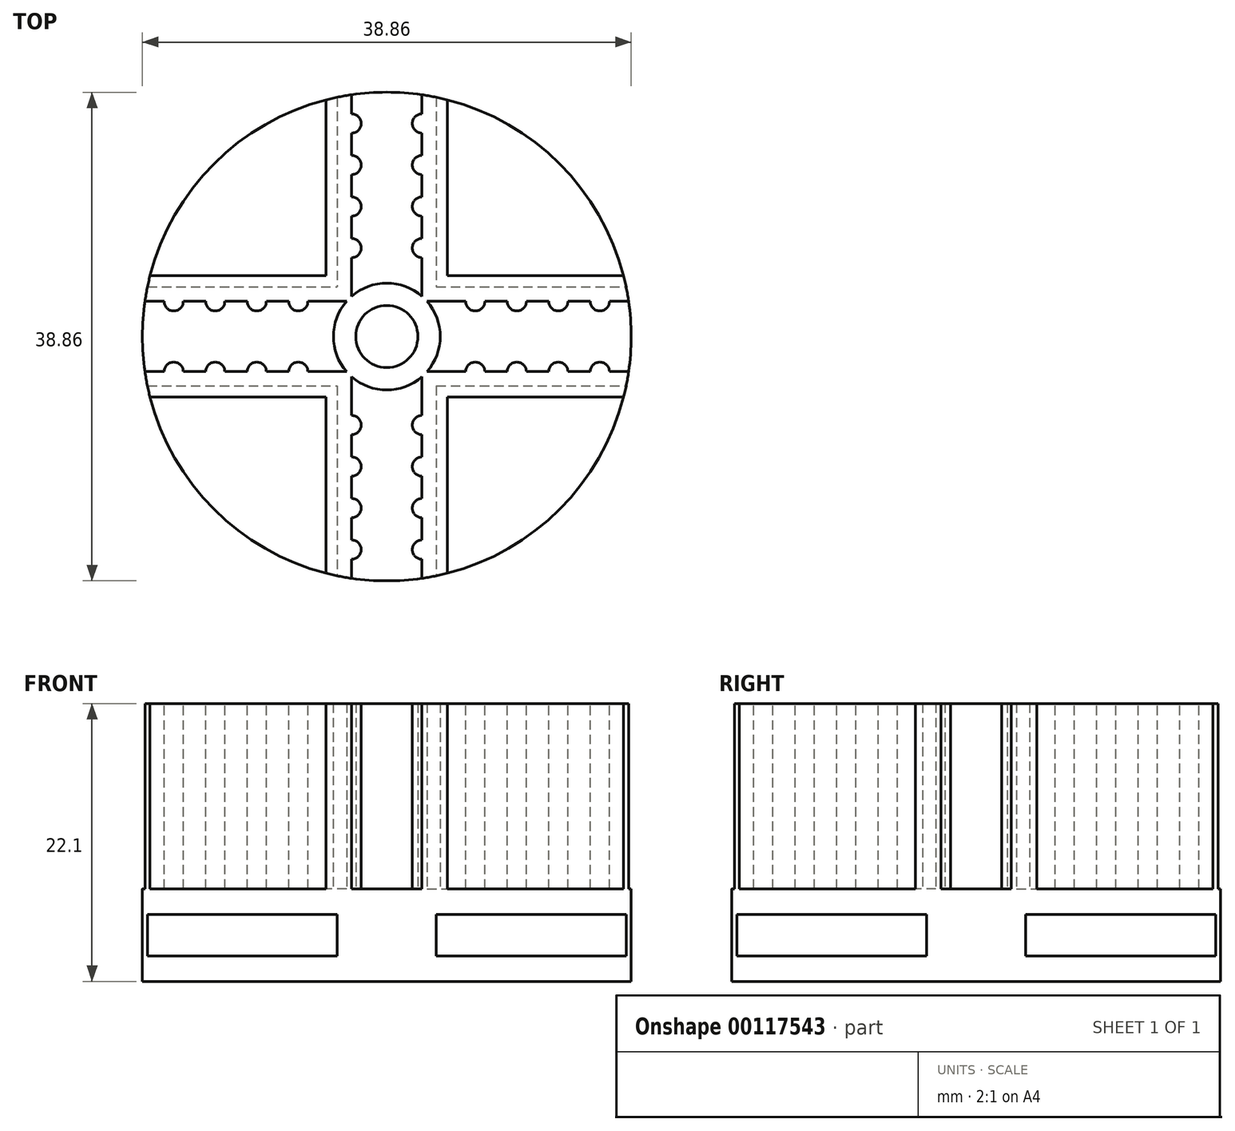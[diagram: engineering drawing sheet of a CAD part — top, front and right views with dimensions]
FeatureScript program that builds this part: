
annotation { "Feature Type Name" : "Feature", "Feature Type Description" : "" }
export const myFeature = defineFeature(function(context is Context, id is Id, definition is map)
    precondition{}
    {
        {
            var Q0;
            Q0=qCreatedBy(makeId("Top.planeOp"),FACE);
            var sketch = newSketch(context, id + "F0", { "sketchPlane" : qUnion([Q0])});
            skCircle(sketch, "E0", {"center": v(0, 0) * mm, "radius": 19.43 * mm});
            skSolve(sketch);
        }
        {
            var Q0;
            Q0 = qSketchRegion(id + "F0", true);
            extrude(context, id + "F1", {"entities" : qUnion([Q0]), "depth" : 2.03 * mm});
        }
        {
            var Q0;
            Q0=makeQuery(id+"F1.opExtrude","CAP_FACE",FACE,{"disambiguationData":[OSD([sQuery(id+"F0.wireOp",EDGE,"E0")])],"isStart":false});
            var sketch = newSketch(context, id + "F2", { "sketchPlane" : qUnion([Q0])});
            skLineSegment(sketch, "E1.left", {"start": v(3.94, 19.03) * mm, "end": v(3.94, 3.94) * mm});
            skLineSegment(sketch, "E1.right", {"start": v(-3.94, 19.03) * mm, "end": v(-3.94, 3.94) * mm});
            skPoint(sketch, "E1.middle", {"position": v(0, 0) * mm});
            skLineSegment(sketch, "E2.bottom", {"start": v(-19.03, 3.94) * mm, "end": v(-3.94, 3.94) * mm});
            skLineSegment(sketch, "E2.top", {"start": v(-19.03, -3.94) * mm, "end": v(-3.94, -3.94) * mm});
            skArc(sketch, "E3.0", {"start": v(19.03, -3.94) * mm, "mid": v(19.43, 0) * mm, "end": v(19.03, 3.94) * mm});
            skLineSegment(sketch, "E4.trimOffspring", {"start": v(3.94, 3.94) * mm, "end": v(19.03, 3.94) * mm});
            skLineSegment(sketch, "E5.trimOffspring", {"start": v(3.94, -3.94) * mm, "end": v(3.94, -19.03) * mm});
            skLineSegment(sketch, "E6.trimOffspring", {"start": v(3.94, -3.94) * mm, "end": v(19.03, -3.94) * mm});
            skLineSegment(sketch, "E7.trimOffspring", {"start": v(-3.94, -3.94) * mm, "end": v(-3.94, -19.03) * mm});
            skArc(sketch, "E8.trimOffspring", {"start": v(3.94, 19.03) * mm, "mid": v(0, 19.43) * mm, "end": v(-3.94, 19.03) * mm});
            skArc(sketch, "E9.trimOffspring", {"start": v(-19.03, 3.94) * mm, "mid": v(-19.43, 0) * mm, "end": v(-19.03, -3.94) * mm});
            skArc(sketch, "E10.trimOffspring", {"start": v(-3.94, -19.03) * mm, "mid": v(0, -19.43) * mm, "end": v(3.94, -19.03) * mm});
            skPoint(sketch, "E11.orphan", {"position": v(-24.75, 3.94) * mm});
            skPoint(sketch, "E12.orphan", {"position": v(-24.75, -3.94) * mm});
            skPoint(sketch, "E1.top.end.orphan", {"position": v(-3.94, -23.72) * mm});
            skPoint(sketch, "E1.top.start.orphan", {"position": v(3.94, -23.72) * mm});
            skPoint(sketch, "E13.orphan", {"position": v(24.75, -3.94) * mm});
            skPoint(sketch, "E14.orphan", {"position": v(24.75, 3.94) * mm});
            skPoint(sketch, "E1.bottom.start.orphan", {"position": v(3.94, 23.72) * mm});
            skPoint(sketch, "E15.orphan", {"position": v(-3.94, 23.72) * mm});
            skLineSegment(sketch, "E16", {"start": v(0, 0) * mm, "end": v(0, 24.04) * mm, "construction": true});
            skPoint(sketch, "E16.endSnap0", {"position": v(0, 19.43) * mm});
            skLineSegment(sketch, "E17", {"start": v(0, 0) * mm, "end": v(36.17, 0) * mm, "construction": true});
            skSolve(sketch);
        }
        {
            var Q0;
            Q0 = qSketchRegion(id + "F2", true);
            extrude(context, id + "F3", {"entities" : qUnion([Q0]), "operationType" : NewBodyOperationType.ADD, "depth" : 5.33 * mm});
        }
        {
            var Q0;
            Q0=makeQuery(id+"F3.opExtrude","CAP_FACE",FACE,{"disambiguationData":[OSD([sQuery(id+"F2.wireOp",EDGE,"E1.left"),sQuery(id+"F2.wireOp",EDGE,"E1.right"),sQuery(id+"F2.wireOp",EDGE,"E2.bottom"),sQuery(id+"F2.wireOp",EDGE,"E2.top"),sQuery(id+"F2.wireOp",EDGE,"E3.0"),sQuery(id+"F2.wireOp",EDGE,"E4.trimOffspring"),sQuery(id+"F2.wireOp",EDGE,"E5.trimOffspring"),sQuery(id+"F2.wireOp",EDGE,"E6.trimOffspring"),sQuery(id+"F2.wireOp",EDGE,"E7.trimOffspring"),sQuery(id+"F2.wireOp",EDGE,"E8.trimOffspring"),sQuery(id+"F2.wireOp",EDGE,"E9.trimOffspring"),sQuery(id+"F2.wireOp",EDGE,"E10.trimOffspring")])],"isStart":false});
            var sketch = newSketch(context, id + "F4", { "sketchPlane" : qUnion([Q0])});
            skPoint(sketch, "E18.center", {"position": v(0, 0) * mm});
            skPoint(sketch, "E19.center", {"position": v(0.66, 0.64) * mm});
            skLineSegment(sketch, "E20", {"start": v(2.8, 19.23) * mm, "end": v(2.8, 2.8) * mm});
            skLineSegment(sketch, "E21", {"start": v(2.8, 2.8) * mm, "end": v(19.23, 2.8) * mm});
            skLineSegment(sketch, "E22", {"start": v(18.82, 4.83) * mm, "end": v(4.83, 4.83) * mm});
            skLineSegment(sketch, "E23", {"start": v(4.83, 4.83) * mm, "end": v(4.83, 18.82) * mm});
            skArc(sketch, "E24.0", {"start": v(19.03, 3.94) * mm, "mid": v(18.93, 4.38) * mm, "end": v(18.82, 4.83) * mm});
            skArc(sketch, "E25.0", {"start": v(3.94, 19.03) * mm, "mid": v(3.37, 19.14) * mm, "end": v(2.8, 19.23) * mm});
            skArc(sketch, "E26.0", {"start": v(19.23, 2.8) * mm, "mid": v(19.14, 3.37) * mm, "end": v(19.03, 3.94) * mm});
            skPoint(sketch, "E27.orphan", {"position": v(-3.94, 19.03) * mm});
            skArc(sketch, "E28.trimOffspring", {"start": v(4.83, 18.82) * mm, "mid": v(4.38, 18.93) * mm, "end": v(3.94, 19.03) * mm});
            skPoint(sketch, "E29.orphan", {"position": v(19.03, -3.94) * mm});
            skLineSegment(sketch, "E30.1.0", {"start": v(-4.83, 18.82) * mm, "end": v(-4.83, 4.83) * mm});
            skLineSegment(sketch, "E30.1.1", {"start": v(-2.8, 2.8) * mm, "end": v(-2.8, 19.23) * mm});
            skLineSegment(sketch, "E30.1.2", {"start": v(-4.83, 4.83) * mm, "end": v(-18.82, 4.83) * mm});
            skLineSegment(sketch, "E30.1.3", {"start": v(-19.23, 2.8) * mm, "end": v(-2.8, 2.8) * mm});
            skArc(sketch, "E30.1.4", {"start": v(-18.82, 4.83) * mm, "mid": v(-18.93, 4.38) * mm, "end": v(-19.03, 3.94) * mm});
            skArc(sketch, "E30.1.5", {"start": v(-2.8, 19.23) * mm, "mid": v(-3.37, 19.14) * mm, "end": v(-3.94, 19.03) * mm});
            skArc(sketch, "E30.1.6", {"start": v(-3.94, 19.03) * mm, "mid": v(-4.38, 18.93) * mm, "end": v(-4.83, 18.82) * mm});
            skArc(sketch, "E30.1.7", {"start": v(-19.03, 3.94) * mm, "mid": v(-19.14, 3.37) * mm, "end": v(-19.23, 2.8) * mm});
            skLineSegment(sketch, "E30.2.0", {"start": v(-18.82, -4.83) * mm, "end": v(-4.83, -4.83) * mm});
            skLineSegment(sketch, "E30.2.1", {"start": v(-2.8, -2.8) * mm, "end": v(-19.23, -2.8) * mm});
            skLineSegment(sketch, "E30.2.2", {"start": v(-4.83, -4.83) * mm, "end": v(-4.83, -18.82) * mm});
            skLineSegment(sketch, "E30.2.3", {"start": v(-2.8, -19.23) * mm, "end": v(-2.8, -2.8) * mm});
            skArc(sketch, "E30.2.4", {"start": v(-4.83, -18.82) * mm, "mid": v(-4.38, -18.93) * mm, "end": v(-3.94, -19.03) * mm});
            skArc(sketch, "E30.2.5", {"start": v(-19.23, -2.8) * mm, "mid": v(-19.14, -3.37) * mm, "end": v(-19.03, -3.94) * mm});
            skArc(sketch, "E30.2.6", {"start": v(-19.03, -3.94) * mm, "mid": v(-18.93, -4.38) * mm, "end": v(-18.82, -4.83) * mm});
            skArc(sketch, "E30.2.7", {"start": v(-3.94, -19.03) * mm, "mid": v(-3.37, -19.14) * mm, "end": v(-2.8, -19.23) * mm});
            skLineSegment(sketch, "E30.3.0", {"start": v(4.83, -18.82) * mm, "end": v(4.83, -4.83) * mm});
            skLineSegment(sketch, "E30.3.1", {"start": v(2.8, -2.8) * mm, "end": v(2.8, -19.23) * mm});
            skLineSegment(sketch, "E30.3.2", {"start": v(4.83, -4.83) * mm, "end": v(18.82, -4.83) * mm});
            skLineSegment(sketch, "E30.3.3", {"start": v(19.23, -2.8) * mm, "end": v(2.8, -2.8) * mm});
            skArc(sketch, "E30.3.4", {"start": v(18.82, -4.83) * mm, "mid": v(18.93, -4.38) * mm, "end": v(19.03, -3.94) * mm});
            skArc(sketch, "E30.3.5", {"start": v(2.8, -19.23) * mm, "mid": v(3.37, -19.14) * mm, "end": v(3.94, -19.03) * mm});
            skArc(sketch, "E30.3.6", {"start": v(3.94, -19.03) * mm, "mid": v(4.38, -18.93) * mm, "end": v(4.83, -18.82) * mm});
            skArc(sketch, "E30.3.7", {"start": v(19.03, -3.94) * mm, "mid": v(19.14, -3.37) * mm, "end": v(19.23, -2.8) * mm});
            skSolve(sketch);
        }
        {
            var Q0;
            Q0 = qSketchRegion(id + "F4", true);
            extrude(context, id + "F5", {"entities" : qUnion([Q0]), "operationType" : NewBodyOperationType.ADD, "depth" : 14.73 * mm});
        }
        {
            var Q0;
            Q0=makeQuery(id+"F3.opExtrude","CAP_FACE",FACE,{"disambiguationData":[OSD([sQuery(id+"F2.wireOp",EDGE,"E1.left"),sQuery(id+"F2.wireOp",EDGE,"E1.right"),sQuery(id+"F2.wireOp",EDGE,"E2.bottom"),sQuery(id+"F2.wireOp",EDGE,"E2.top"),sQuery(id+"F2.wireOp",EDGE,"E3.0"),sQuery(id+"F2.wireOp",EDGE,"E4.trimOffspring"),sQuery(id+"F2.wireOp",EDGE,"E5.trimOffspring"),sQuery(id+"F2.wireOp",EDGE,"E6.trimOffspring"),sQuery(id+"F2.wireOp",EDGE,"E7.trimOffspring"),sQuery(id+"F2.wireOp",EDGE,"E8.trimOffspring"),sQuery(id+"F2.wireOp",EDGE,"E9.trimOffspring"),sQuery(id+"F2.wireOp",EDGE,"E10.trimOffspring")])],"isStart":false});
            var sketch = newSketch(context, id + "F6", { "sketchPlane" : qUnion([Q0])});
            skCircle(sketch, "E31", {"center": v(0, 0) * mm, "radius": 2.47 * mm});
            skCircle(sketch, "E32", {"center": v(0, 0) * mm, "radius": 4.25 * mm});
            skSolve(sketch);
        }
        {
            var Q0;
            Q0 = qSketchRegion(id + "F6", true);
            var Q1;
            Q1=makeQuery(id+"F5.opExtrude","CAP_FACE",FACE,{"disambiguationData":[OSD([sQuery(id+"F4.wireOp",EDGE,"E30.1.0"),sQuery(id+"F4.wireOp",EDGE,"E30.1.1"),sQuery(id+"F4.wireOp",EDGE,"E30.1.2"),sQuery(id+"F4.wireOp",EDGE,"E30.1.3"),sQuery(id+"F4.wireOp",EDGE,"E30.1.4"),sQuery(id+"F4.wireOp",EDGE,"E30.1.5"),sQuery(id+"F4.wireOp",EDGE,"E30.1.6"),sQuery(id+"F4.wireOp",EDGE,"E30.1.7")])],"isStart":false});
            extrude(context, id + "F7", {"entities" : qUnion([Q0]), "operationType" : NewBodyOperationType.ADD, "endBound" : BoundingType.UP_TO_SURFACE, "endBoundEntityFace" : qUnion([Q1]), "depth" : 25.4 * mm});
        }
        {
            var Q0;
            Q0=makeQuery(id+"F5.opExtrude","CAP_FACE",FACE,{"disambiguationData":[OSD([sQuery(id+"F4.wireOp",EDGE,"E20"),sQuery(id+"F4.wireOp",EDGE,"E21"),sQuery(id+"F4.wireOp",EDGE,"E22"),sQuery(id+"F4.wireOp",EDGE,"E23"),sQuery(id+"F4.wireOp",EDGE,"E24.0"),sQuery(id+"F4.wireOp",EDGE,"E25.0"),sQuery(id+"F4.wireOp",EDGE,"E26.0"),sQuery(id+"F4.wireOp",EDGE,"E28.trimOffspring")])],"isStart":true});
            var sketch = newSketch(context, id + "F8", { "sketchPlane" : qUnion([Q0])});
            skLineSegment(sketch, "E33.0.0", {"start": v(-3.94, 19.03) * mm, "end": v(-3.94, 3.94) * mm});
            skLineSegment(sketch, "E33.0.1", {"start": v(-3.94, 3.94) * mm, "end": v(-19.03, 3.94) * mm});
            skArc(sketch, "E33.0.2", {"start": v(-19.03, 3.94) * mm, "mid": v(-13.74, 13.74) * mm, "end": v(-3.94, 19.03) * mm});
            skArc(sketch, "E34.1.0", {"start": v(-3.94, -19.03) * mm, "mid": v(-13.74, -13.74) * mm, "end": v(-19.03, -3.94) * mm});
            skLineSegment(sketch, "E34.1.1", {"start": v(-3.94, -3.94) * mm, "end": v(-3.94, -19.03) * mm});
            skLineSegment(sketch, "E34.1.2", {"start": v(-19.03, -3.94) * mm, "end": v(-3.94, -3.94) * mm});
            skArc(sketch, "E34.2.0", {"start": v(19.03, -3.94) * mm, "mid": v(13.74, -13.74) * mm, "end": v(3.94, -19.03) * mm});
            skLineSegment(sketch, "E34.2.1", {"start": v(3.94, -3.94) * mm, "end": v(19.03, -3.94) * mm});
            skLineSegment(sketch, "E34.2.2", {"start": v(3.94, -19.03) * mm, "end": v(3.94, -3.94) * mm});
            skArc(sketch, "E34.3.0", {"start": v(3.94, 19.03) * mm, "mid": v(13.74, 13.74) * mm, "end": v(19.03, 3.94) * mm});
            skLineSegment(sketch, "E34.3.1", {"start": v(3.94, 3.94) * mm, "end": v(3.94, 19.03) * mm});
            skLineSegment(sketch, "E34.3.2", {"start": v(19.03, 3.94) * mm, "end": v(3.94, 3.94) * mm});
            skSolve(sketch);
        }
        {
            var Q0;
            Q0 = qSketchRegion(id + "F8", true);
            extrude(context, id + "F9", {"entities" : qUnion([Q0]), "operationType" : NewBodyOperationType.ADD, "depth" : 2.03 * mm});
        }
        {
            var Q0;
            {var subQ0=sQuery(id+"F4.wireOp",EDGE,"E30.1.7");var subQ1=sQuery(id+"F4.wireOp",EDGE,"E30.1.6");var subQ2=sQuery(id+"F4.wireOp",EDGE,"E30.1.5");var subQ3=sQuery(id+"F4.wireOp",EDGE,"E30.1.4");var subQ4=sQuery(id+"F4.wireOp",EDGE,"E30.1.3");var subQ5=sQuery(id+"F4.wireOp",EDGE,"E30.1.2");var subQ6=sQuery(id+"F4.wireOp",EDGE,"E30.1.1");var subQ7=sQuery(id+"F4.wireOp",EDGE,"E30.1.0");Q0=makeQuery(id+"F7.boolean.opBoolean","MERGE",FACE,{"derivedFrom":[makeQuery(id+"F5.opExtrude","CAP_FACE",FACE,{"disambiguationData":[OSD([sQuery(id+"F4.wireOp",EDGE,"E20"),sQuery(id+"F4.wireOp",EDGE,"E21"),sQuery(id+"F4.wireOp",EDGE,"E22"),sQuery(id+"F4.wireOp",EDGE,"E23"),sQuery(id+"F4.wireOp",EDGE,"E24.0"),sQuery(id+"F4.wireOp",EDGE,"E25.0"),sQuery(id+"F4.wireOp",EDGE,"E26.0"),sQuery(id+"F4.wireOp",EDGE,"E28.trimOffspring")])],"isStart":false}),makeQuery(id+"F5.opExtrude","CAP_FACE",FACE,{"disambiguationData":[OSD([subQ7,subQ6,subQ5,subQ4,subQ3,subQ2,subQ1,subQ0])],"isStart":false}),makeQuery(id+"F5.opExtrude","CAP_FACE",FACE,{"disambiguationData":[OSD([sQuery(id+"F4.wireOp",EDGE,"E30.2.0"),sQuery(id+"F4.wireOp",EDGE,"E30.2.1"),sQuery(id+"F4.wireOp",EDGE,"E30.2.2"),sQuery(id+"F4.wireOp",EDGE,"E30.2.3"),sQuery(id+"F4.wireOp",EDGE,"E30.2.4"),sQuery(id+"F4.wireOp",EDGE,"E30.2.5"),sQuery(id+"F4.wireOp",EDGE,"E30.2.6"),sQuery(id+"F4.wireOp",EDGE,"E30.2.7")])],"isStart":false}),makeQuery(id+"F5.opExtrude","CAP_FACE",FACE,{"disambiguationData":[OSD([sQuery(id+"F4.wireOp",EDGE,"E30.3.0"),sQuery(id+"F4.wireOp",EDGE,"E30.3.1"),sQuery(id+"F4.wireOp",EDGE,"E30.3.2"),sQuery(id+"F4.wireOp",EDGE,"E30.3.3"),sQuery(id+"F4.wireOp",EDGE,"E30.3.4"),sQuery(id+"F4.wireOp",EDGE,"E30.3.5"),sQuery(id+"F4.wireOp",EDGE,"E30.3.6"),sQuery(id+"F4.wireOp",EDGE,"E30.3.7")])],"isStart":false}),makeQuery(id+"F7.opExtrude","CAP_FACE",FACE,{"disambiguationData":[OSD([subQ7,subQ6,subQ5,subQ4,subQ3,subQ2,subQ1,subQ0])],"isStart":false})]});}
            var sketch = newSketch(context, id + "F10", { "sketchPlane" : qUnion([Q0])});
            skLineSegment(sketch, "E35.0", {"start": v(17.7, -2.8) * mm, "end": v(16.18, -2.8) * mm});
            skArc(sketch, "E36", {"start": v(17.7, -2.8) * mm, "mid": v(16.94, -2.03) * mm, "end": v(16.18, -2.8) * mm});
            skPoint(sketch, "E37.orphan", {"position": v(19.23, -2.8) * mm});
            skPoint(sketch, "E38.orphan", {"position": v(3.2, -2.8) * mm});
            skArc(sketch, "E39.1.0.0", {"start": v(14.4, -2.8) * mm, "mid": v(13.64, -2.03) * mm, "end": v(12.88, -2.8) * mm});
            skPoint(sketch, "E39.1.0.1", {"position": v(15.93, -2.8) * mm});
            skLineSegment(sketch, "E39.1.0.2", {"start": v(14.4, -2.8) * mm, "end": v(12.88, -2.8) * mm});
            skArc(sketch, "E39.2.0.0", {"start": v(11.1, -2.8) * mm, "mid": v(10.34, -2.03) * mm, "end": v(9.58, -2.8) * mm});
            skPoint(sketch, "E39.2.0.1", {"position": v(12.63, -2.8) * mm});
            skLineSegment(sketch, "E39.2.0.2", {"start": v(11.1, -2.8) * mm, "end": v(9.58, -2.8) * mm});
            skArc(sketch, "E39.3.0.0", {"start": v(7.8, -2.8) * mm, "mid": v(7.04, -2.03) * mm, "end": v(6.28, -2.8) * mm});
            skPoint(sketch, "E39.3.0.1", {"position": v(9.32, -2.8) * mm});
            skLineSegment(sketch, "E39.3.0.2", {"start": v(7.8, -2.8) * mm, "end": v(6.28, -2.8) * mm});
            skLineSegment(sketch, "E39.direction1", {"start": v(16.18, -2.8) * mm, "end": v(12.88, -2.8) * mm, "construction": true});
            skLineSegment(sketch, "E40", {"start": v(0, 0) * mm, "end": v(26.06, 0) * mm, "construction": true});
            skLineSegment(sketch, "E41.MirrorCS", {"start": v(17.7, 2.8) * mm, "end": v(16.18, 2.8) * mm});
            skLineSegment(sketch, "E42.MirrorCS", {"start": v(7.8, 2.8) * mm, "end": v(6.28, 2.8) * mm});
            skLineSegment(sketch, "E43.MirrorCS", {"start": v(14.4, 2.8) * mm, "end": v(12.88, 2.8) * mm});
            skLineSegment(sketch, "E44.MirrorCS", {"start": v(11.1, 2.8) * mm, "end": v(9.58, 2.8) * mm});
            skArc(sketch, "E45.MirrorCS", {"start": v(17.7, 2.8) * mm, "mid": v(16.94, 2.03) * mm, "end": v(16.18, 2.8) * mm});
            skPoint(sketch, "E46.MirrorP", {"position": v(15.93, 2.8) * mm});
            skPoint(sketch, "E47.MirrorP", {"position": v(12.63, 2.8) * mm});
            skPoint(sketch, "E48.MirrorP", {"position": v(19.23, 2.8) * mm});
            skArc(sketch, "E49.MirrorCS", {"start": v(11.1, 2.8) * mm, "mid": v(10.34, 2.03) * mm, "end": v(9.58, 2.8) * mm});
            skPoint(sketch, "E50.MirrorP", {"position": v(9.32, 2.8) * mm});
            skLineSegment(sketch, "E51.MirrorCS", {"start": v(16.18, 2.8) * mm, "end": v(12.88, 2.8) * mm, "construction": true});
            skArc(sketch, "E52.MirrorCS", {"start": v(14.4, 2.8) * mm, "mid": v(13.64, 2.03) * mm, "end": v(12.88, 2.8) * mm});
            skArc(sketch, "E53.MirrorCS", {"start": v(7.8, 2.8) * mm, "mid": v(7.04, 2.03) * mm, "end": v(6.28, 2.8) * mm});
            skLineSegment(sketch, "E54.1.0", {"start": v(-2.8, 16.18) * mm, "end": v(-2.8, 12.88) * mm, "construction": true});
            skPoint(sketch, "E54.1.1", {"position": v(2.8, 19.23) * mm});
            skArc(sketch, "E54.1.2", {"start": v(2.8, 11.1) * mm, "mid": v(2.03, 10.34) * mm, "end": v(2.8, 9.58) * mm});
            skPoint(sketch, "E54.1.3", {"position": v(2.8, 15.93) * mm});
            skArc(sketch, "E54.1.4", {"start": v(-2.8, 11.1) * mm, "mid": v(-2.03, 10.34) * mm, "end": v(-2.8, 9.58) * mm});
            skArc(sketch, "E54.1.5", {"start": v(2.8, 7.8) * mm, "mid": v(2.03, 7.04) * mm, "end": v(2.8, 6.28) * mm});
            skArc(sketch, "E54.1.6", {"start": v(2.8, 17.7) * mm, "mid": v(2.03, 16.94) * mm, "end": v(2.8, 16.18) * mm});
            skPoint(sketch, "E54.1.7", {"position": v(2.8, 9.32) * mm});
            skPoint(sketch, "E54.1.8", {"position": v(-2.8, 12.63) * mm});
            skArc(sketch, "E54.1.9", {"start": v(-2.8, 17.7) * mm, "mid": v(-2.03, 16.94) * mm, "end": v(-2.8, 16.18) * mm});
            skPoint(sketch, "E54.1.10", {"position": v(-2.8, 19.23) * mm});
            skPoint(sketch, "E54.1.11", {"position": v(2.8, 12.63) * mm});
            skLineSegment(sketch, "E54.1.12", {"start": v(0, 0) * mm, "end": v(0, 26.06) * mm, "construction": true});
            skPoint(sketch, "E54.1.13", {"position": v(-2.8, 9.32) * mm});
            skArc(sketch, "E54.1.14", {"start": v(-2.8, 7.8) * mm, "mid": v(-2.03, 7.04) * mm, "end": v(-2.8, 6.28) * mm});
            skArc(sketch, "E54.1.15", {"start": v(2.8, 14.4) * mm, "mid": v(2.03, 13.64) * mm, "end": v(2.8, 12.88) * mm});
            skLineSegment(sketch, "E54.1.16", {"start": v(2.8, 16.18) * mm, "end": v(2.8, 12.88) * mm, "construction": true});
            skArc(sketch, "E54.1.17", {"start": v(-2.8, 14.4) * mm, "mid": v(-2.03, 13.64) * mm, "end": v(-2.8, 12.88) * mm});
            skPoint(sketch, "E54.1.18", {"position": v(-2.8, 15.93) * mm});
            skLineSegment(sketch, "E54.1.19", {"start": v(2.8, 11.1) * mm, "end": v(2.8, 9.58) * mm});
            skLineSegment(sketch, "E54.1.20", {"start": v(-2.8, 17.7) * mm, "end": v(-2.8, 16.18) * mm});
            skLineSegment(sketch, "E54.1.21", {"start": v(-2.8, 7.8) * mm, "end": v(-2.8, 6.28) * mm});
            skLineSegment(sketch, "E54.1.22", {"start": v(-2.8, 14.4) * mm, "end": v(-2.8, 12.88) * mm});
            skLineSegment(sketch, "E54.1.23", {"start": v(2.8, 17.7) * mm, "end": v(2.8, 16.18) * mm});
            skLineSegment(sketch, "E54.1.24", {"start": v(-2.8, 11.1) * mm, "end": v(-2.8, 9.58) * mm});
            skLineSegment(sketch, "E54.1.25", {"start": v(2.8, 14.4) * mm, "end": v(2.8, 12.88) * mm});
            skLineSegment(sketch, "E54.1.26", {"start": v(2.8, 7.8) * mm, "end": v(2.8, 6.28) * mm});
            skLineSegment(sketch, "E54.2.0", {"start": v(-16.18, -2.8) * mm, "end": v(-12.88, -2.8) * mm, "construction": true});
            skPoint(sketch, "E54.2.1", {"position": v(-19.23, 2.8) * mm});
            skArc(sketch, "E54.2.2", {"start": v(-11.1, 2.8) * mm, "mid": v(-10.34, 2.03) * mm, "end": v(-9.58, 2.8) * mm});
            skPoint(sketch, "E54.2.3", {"position": v(-15.93, 2.8) * mm});
            skArc(sketch, "E54.2.4", {"start": v(-11.1, -2.8) * mm, "mid": v(-10.34, -2.03) * mm, "end": v(-9.58, -2.8) * mm});
            skArc(sketch, "E54.2.5", {"start": v(-7.8, 2.8) * mm, "mid": v(-7.04, 2.03) * mm, "end": v(-6.28, 2.8) * mm});
            skArc(sketch, "E54.2.6", {"start": v(-17.7, 2.8) * mm, "mid": v(-16.94, 2.03) * mm, "end": v(-16.18, 2.8) * mm});
            skPoint(sketch, "E54.2.7", {"position": v(-9.32, 2.8) * mm});
            skPoint(sketch, "E54.2.8", {"position": v(-12.63, -2.8) * mm});
            skArc(sketch, "E54.2.9", {"start": v(-17.7, -2.8) * mm, "mid": v(-16.94, -2.03) * mm, "end": v(-16.18, -2.8) * mm});
            skPoint(sketch, "E54.2.10", {"position": v(-19.23, -2.8) * mm});
            skPoint(sketch, "E54.2.11", {"position": v(-12.63, 2.8) * mm});
            skLineSegment(sketch, "E54.2.12", {"start": v(0, 0) * mm, "end": v(-26.06, 0) * mm, "construction": true});
            skPoint(sketch, "E54.2.13", {"position": v(-9.32, -2.8) * mm});
            skArc(sketch, "E54.2.14", {"start": v(-7.8, -2.8) * mm, "mid": v(-7.04, -2.03) * mm, "end": v(-6.28, -2.8) * mm});
            skArc(sketch, "E54.2.15", {"start": v(-14.4, 2.8) * mm, "mid": v(-13.64, 2.03) * mm, "end": v(-12.88, 2.8) * mm});
            skLineSegment(sketch, "E54.2.16", {"start": v(-16.18, 2.8) * mm, "end": v(-12.88, 2.8) * mm, "construction": true});
            skArc(sketch, "E54.2.17", {"start": v(-14.4, -2.8) * mm, "mid": v(-13.64, -2.03) * mm, "end": v(-12.88, -2.8) * mm});
            skPoint(sketch, "E54.2.18", {"position": v(-15.93, -2.8) * mm});
            skLineSegment(sketch, "E54.2.19", {"start": v(-11.1, 2.8) * mm, "end": v(-9.58, 2.8) * mm});
            skLineSegment(sketch, "E54.2.20", {"start": v(-17.7, -2.8) * mm, "end": v(-16.18, -2.8) * mm});
            skLineSegment(sketch, "E54.2.21", {"start": v(-7.8, -2.8) * mm, "end": v(-6.28, -2.8) * mm});
            skLineSegment(sketch, "E54.2.22", {"start": v(-14.4, -2.8) * mm, "end": v(-12.88, -2.8) * mm});
            skLineSegment(sketch, "E54.2.23", {"start": v(-17.7, 2.8) * mm, "end": v(-16.18, 2.8) * mm});
            skLineSegment(sketch, "E54.2.24", {"start": v(-11.1, -2.8) * mm, "end": v(-9.58, -2.8) * mm});
            skLineSegment(sketch, "E54.2.25", {"start": v(-14.4, 2.8) * mm, "end": v(-12.88, 2.8) * mm});
            skLineSegment(sketch, "E54.2.26", {"start": v(-7.8, 2.8) * mm, "end": v(-6.28, 2.8) * mm});
            skLineSegment(sketch, "E54.3.0", {"start": v(2.8, -16.18) * mm, "end": v(2.8, -12.88) * mm, "construction": true});
            skPoint(sketch, "E54.3.1", {"position": v(-2.8, -19.23) * mm});
            skArc(sketch, "E54.3.2", {"start": v(-2.8, -11.1) * mm, "mid": v(-2.03, -10.34) * mm, "end": v(-2.8, -9.58) * mm});
            skPoint(sketch, "E54.3.3", {"position": v(-2.8, -15.93) * mm});
            skArc(sketch, "E54.3.4", {"start": v(2.8, -11.1) * mm, "mid": v(2.03, -10.34) * mm, "end": v(2.8, -9.58) * mm});
            skArc(sketch, "E54.3.5", {"start": v(-2.8, -7.8) * mm, "mid": v(-2.03, -7.04) * mm, "end": v(-2.8, -6.28) * mm});
            skArc(sketch, "E54.3.6", {"start": v(-2.8, -17.7) * mm, "mid": v(-2.03, -16.94) * mm, "end": v(-2.8, -16.18) * mm});
            skPoint(sketch, "E54.3.7", {"position": v(-2.8, -9.32) * mm});
            skPoint(sketch, "E54.3.8", {"position": v(2.8, -12.63) * mm});
            skArc(sketch, "E54.3.9", {"start": v(2.8, -17.7) * mm, "mid": v(2.03, -16.94) * mm, "end": v(2.8, -16.18) * mm});
            skPoint(sketch, "E54.3.10", {"position": v(2.8, -19.23) * mm});
            skPoint(sketch, "E54.3.11", {"position": v(-2.8, -12.63) * mm});
            skLineSegment(sketch, "E54.3.12", {"start": v(0, 0) * mm, "end": v(0, -26.06) * mm, "construction": true});
            skPoint(sketch, "E54.3.13", {"position": v(2.8, -9.32) * mm});
            skArc(sketch, "E54.3.14", {"start": v(2.8, -7.8) * mm, "mid": v(2.03, -7.04) * mm, "end": v(2.8, -6.28) * mm});
            skArc(sketch, "E54.3.15", {"start": v(-2.8, -14.4) * mm, "mid": v(-2.03, -13.64) * mm, "end": v(-2.8, -12.88) * mm});
            skLineSegment(sketch, "E54.3.16", {"start": v(-2.8, -16.18) * mm, "end": v(-2.8, -12.88) * mm, "construction": true});
            skArc(sketch, "E54.3.17", {"start": v(2.8, -14.4) * mm, "mid": v(2.03, -13.64) * mm, "end": v(2.8, -12.88) * mm});
            skPoint(sketch, "E54.3.18", {"position": v(2.8, -15.93) * mm});
            skLineSegment(sketch, "E54.3.19", {"start": v(-2.8, -11.1) * mm, "end": v(-2.8, -9.58) * mm});
            skLineSegment(sketch, "E54.3.20", {"start": v(2.8, -17.7) * mm, "end": v(2.8, -16.18) * mm});
            skLineSegment(sketch, "E54.3.21", {"start": v(2.8, -7.8) * mm, "end": v(2.8, -6.28) * mm});
            skLineSegment(sketch, "E54.3.22", {"start": v(2.8, -14.4) * mm, "end": v(2.8, -12.88) * mm});
            skLineSegment(sketch, "E54.3.23", {"start": v(-2.8, -17.7) * mm, "end": v(-2.8, -16.18) * mm});
            skLineSegment(sketch, "E54.3.24", {"start": v(2.8, -11.1) * mm, "end": v(2.8, -9.58) * mm});
            skLineSegment(sketch, "E54.3.25", {"start": v(-2.8, -14.4) * mm, "end": v(-2.8, -12.88) * mm});
            skLineSegment(sketch, "E54.3.26", {"start": v(-2.8, -7.8) * mm, "end": v(-2.8, -6.28) * mm});
            skPoint(sketch, "E54.center", {"position": v(0, 0) * mm});
            skSolve(sketch);
        }
        {
            var Q0;
            Q0 = qSketchRegion(id + "F10", true);
            extrude(context, id + "F11", {"entities" : qUnion([Q0]), "operationType" : NewBodyOperationType.ADD, "endBound" : BoundingType.UP_TO_NEXT, "oppositeDirection" : true, "depth" : 25.4 * mm});
        }
    });
